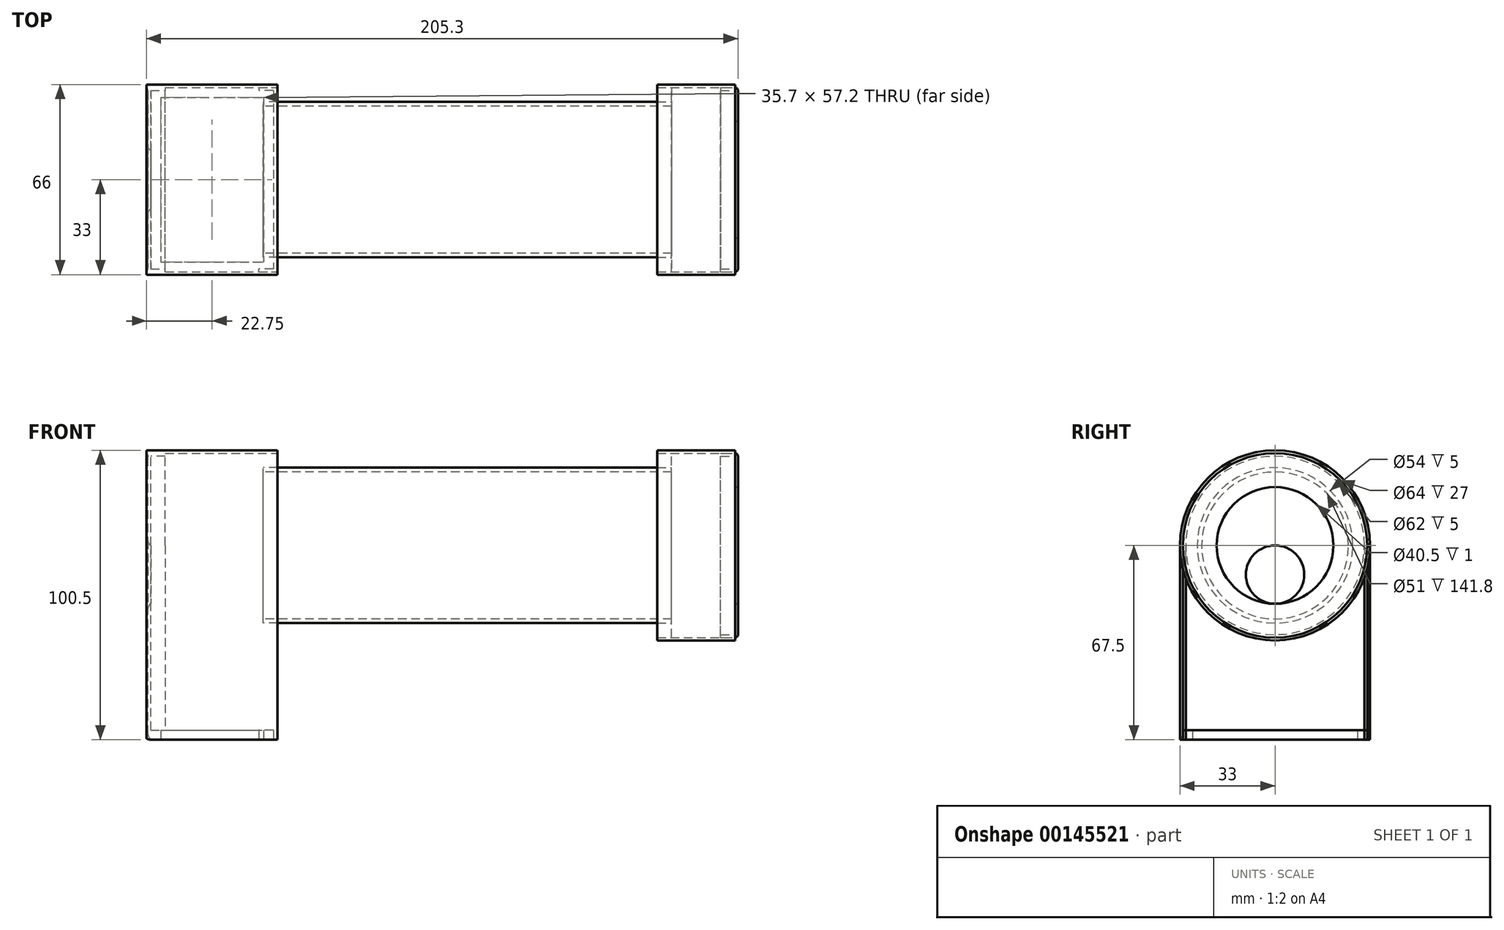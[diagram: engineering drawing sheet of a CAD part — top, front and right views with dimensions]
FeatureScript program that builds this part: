
annotation { "Feature Type Name" : "Feature", "Feature Type Description" : "" }
export const myFeature = defineFeature(function(context is Context, id is Id, definition is map)
    precondition{}
    {
        {
            assignVariable(context, id + "F0", {"name" : "CuBlech10", "anyValue" : 1});
        }
        {
            var Q0;
            Q0=qCreatedBy(makeId("Right.planeOp"),FACE);
            var sketch = newSketch(context, id + "F1", { "sketchPlane" : qUnion([Q0])});
            skCircle(sketch, "E0", {"center": v(0, 0) * mm, "radius": 27 * mm});
            skCircle(sketch, "E1", {"center": v(0, 0) * mm, "radius": 25.5 * mm});
            skSolve(sketch);
        }
        {
            var Q0;
            Q0 = qSketchRegion(id + "F1", true);
            extrude(context, id + "F2", {"entities" : qUnion([Q0]), "depth" : 141.8 * mm});
        }
        {
            var Q0;
            Q0=makeQuery(id+"F2.opExtrude","CAP_FACE",FACE,{"disambiguationData":[OSD([sQuery(id+"F1.wireOp",EDGE,"E0"),sQuery(id+"F1.wireOp",EDGE,"E1")])],"isStart":true});
            var sketch = newSketch(context, id + "F3", { "sketchPlane" : qUnion([Q0])});
            skLineSegment(sketch, "E2", {"start": v(-23.38, -13.5) * mm, "end": v(-22.08, -12.75) * mm});
            skLineSegment(sketch, "E3", {"start": v(22.08, -12.75) * mm, "end": v(23.38, -13.5) * mm});
            skLineSegment(sketch, "E4", {"start": v(0, 0) * mm, "end": v(0, -29.7) * mm, "construction": true});
            skArc(sketch, "E5", {"start": v(-22.08, -12.75) * mm, "mid": v(0, -25.5) * mm, "end": v(22.08, -12.75) * mm});
            skArc(sketch, "E6", {"start": v(-23.38, -13.5) * mm, "mid": v(0, -27) * mm, "end": v(23.38, -13.5) * mm});
            skSolve(sketch);
        }
        {
            var Q0;
            Q0=qCreatedBy(makeId("Front.planeOp"),FACE);
            var sketch = newSketch(context, id + "F4", { "sketchPlane" : qUnion([Q0])});
            skLineSegment(sketch, "E7", {"start": v(172.96, 0) * mm, "end": v(133.05, 0) * mm, "construction": true});
            skLineSegment(sketch, "E8.bottom", {"start": v(136.8, 32) * mm, "end": v(141.8, 32) * mm});
            skLineSegment(sketch, "E8.top", {"start": v(136.8, 27) * mm, "end": v(141.8, 27) * mm});
            skLineSegment(sketch, "E8.left", {"start": v(136.8, 32) * mm, "end": v(136.8, 27) * mm});
            skLineSegment(sketch, "E8.right", {"start": v(141.8, 32) * mm, "end": v(141.8, 27) * mm});
            skLineSegment(sketch, "E9.top", {"start": v(136.8, 33) * mm, "end": v(163.8, 33) * mm});
            skLineSegment(sketch, "E9.left", {"start": v(136.8, 32) * mm, "end": v(136.8, 33) * mm});
            skLineSegment(sketch, "E9.right", {"start": v(163.8, 32) * mm, "end": v(163.8, 33) * mm});
            skLineSegment(sketch, "E10.top", {"start": v(164.8, 20.25) * mm, "end": v(163.8, 20.25) * mm});
            skLineSegment(sketch, "E10.left", {"start": v(164.8, 32) * mm, "end": v(164.8, 20.25) * mm});
            skLineSegment(sketch, "E10.right", {"start": v(158.8, 32) * mm, "end": v(158.8, 31) * mm});
            skLineSegment(sketch, "E11.top", {"start": v(158.8, 31) * mm, "end": v(163.8, 31) * mm});
            skLineSegment(sketch, "E11.right", {"start": v(163.8, 20.25) * mm, "end": v(163.8, 31) * mm});
            skLineSegment(sketch, "E12", {"start": v(158.8, 32) * mm, "end": v(164.8, 32) * mm});
            skLineSegment(sketch, "E13", {"start": v(163.8, 32) * mm, "end": v(136.8, 32) * mm});
            skSolve(sketch);
        }
        {
            var Q0;
            Q0=makeQuery(id+"F4.imprint","IMPRINT",FACE,{"disambiguationData":[TD([[makeQuery(id+"F4.imprint","IMPRINT",EDGE,{"derivedFrom":sQuery(id+"F4.wireOp",EDGE,"E8.top")}),1.0]])]});
            var Q1;
            Q1=sQuery(id+"F4.wireOp",EDGE,"E7");
            revolve(context, id + "F5", {"entities" : qUnion([Q0]), "axis" : qUnion([Q1]), "revolveType" : RevolveType.FULL});
        }
        {
            var Q0;
            Q0=makeQuery(id+"F4.imprint","IMPRINT",FACE,{"disambiguationData":[TD([[makeQuery(id+"F4.imprint","IMPRINT",EDGE,{"derivedFrom":sQuery(id+"F4.wireOp",EDGE,"E9.top")}),-1.0]])]});
            var Q1;
            Q1=sQuery(id+"F4.wireOp",EDGE,"E7");
            revolve(context, id + "F6", {"entities" : qUnion([Q0]), "axis" : qUnion([Q1]), "revolveType" : RevolveType.FULL});
        }
        {
            var Q0;
            Q0=makeQuery(id+"F4.imprint","IMPRINT",FACE,{"disambiguationData":[TD([[makeQuery(id+"F4.imprint","IMPRINT",EDGE,{"derivedFrom":sQuery(id+"F4.wireOp",EDGE,"E10.top")}),-1.0]])]});
            var Q1;
            Q1=sQuery(id+"F4.wireOp",EDGE,"E7");
            revolve(context, id + "F7", {"entities" : qUnion([Q0]), "axis" : qUnion([Q1]), "revolveType" : RevolveType.FULL});
        }
        {
            var Q0;
            Q0=makeQuery(id+"F7.opRevolve","SWEPT_EDGE",EDGE,{"disambiguationData":[OSD([sQuery(id+"F4.wireOp",EDGE,"E10.left"),sQuery(id+"F4.wireOp",EDGE,"E12")])]});
            fillet(context, id + "F8", {"entities" : qUnion([Q0]), "radius" : 1 * mm, "tangentPropagation" : true, "allowEdgeOverflow" : false});
        }
        {
            var Q0;
            Q0=makeQuery(id+"F2.opExtrude","CAP_FACE",FACE,{"disambiguationData":[OSD([sQuery(id+"F1.wireOp",EDGE,"E0"),sQuery(id+"F1.wireOp",EDGE,"E1")])],"isStart":true});
            cPlane(context, id + "F9", {"entities" : qUnion([Q0]), "cplaneType" : CPlaneType.OFFSET, "offset" : 5 * mm, "oppositeDirection" : true, "width" : 150 * mm, "height" : 150 * mm});
        }
        {
            var Q0;
            Q0=qCreatedBy(id+"F9.planeOp",FACE);
            var sketch = newSketch(context, id + "F10", { "sketchPlane" : qUnion([Q0])});
            skArc(sketch, "E14", {"start": v(32, 0) * mm, "mid": v(0, 32) * mm, "end": v(-32, 0) * mm});
            skArc(sketch, "E15", {"start": v(33, 0) * mm, "mid": v(0, 33) * mm, "end": v(-33, 0) * mm});
            skLineSegment(sketch, "E16", {"start": v(-31.44, 0) * mm, "end": v(31.77, 0) * mm, "construction": true});
            skLineSegment(sketch, "E17.bottom", {"start": v(-33, 0) * mm, "end": v(-32, 0) * mm});
            skLineSegment(sketch, "E17.top", {"start": v(-33, -67.5) * mm, "end": v(-32, -67.5) * mm});
            skLineSegment(sketch, "E17.left", {"start": v(-33, 0) * mm, "end": v(-33, -67.5) * mm});
            skLineSegment(sketch, "E17.right", {"start": v(-32, 0) * mm, "end": v(-32, -67.5) * mm});
            skLineSegment(sketch, "E18.bottom", {"start": v(33, 0) * mm, "end": v(32, 0) * mm});
            skLineSegment(sketch, "E18.top", {"start": v(33, -67.5) * mm, "end": v(32, -67.5) * mm});
            skLineSegment(sketch, "E18.left", {"start": v(33, 0) * mm, "end": v(33, -67.5) * mm});
            skLineSegment(sketch, "E18.right", {"start": v(32, 0) * mm, "end": v(32, -67.5) * mm});
            skSolve(sketch);
        }
        {
            var Q0;
            Q0 = qSketchRegion(id + "F10", true);
            extrude(context, id + "F11", {"entities" : qUnion([Q0]), "depth" : 45.5 * mm});
        }
        {
            var Q0;
            Q0=makeQuery(id+"F11.opExtrude","SWEPT_FACE",FACE,{"disambiguationData":[OSD([sQuery(id+"F10.wireOp",EDGE,"E18.top")])]});
            var sketch = newSketch(context, id + "F12", { "sketchPlane" : qUnion([Q0])});
            skLineSegment(sketch, "E19.bottom", {"start": v(-39, -32) * mm, "end": v(3.5, -32) * mm});
            skLineSegment(sketch, "E19.top", {"start": v(-39, 32) * mm, "end": v(3.5, 32) * mm});
            skLineSegment(sketch, "E19.left", {"start": v(-39, -32) * mm, "end": v(-39, 32) * mm});
            skLineSegment(sketch, "E19.right", {"start": v(3.5, -32) * mm, "end": v(3.5, 32) * mm});
            skLineSegment(sketch, "E20.bottom", {"start": v(-35.6, -28.6) * mm, "end": v(0.1, -28.6) * mm});
            skLineSegment(sketch, "E20.top", {"start": v(-35.6, 28.6) * mm, "end": v(0.1, 28.6) * mm});
            skLineSegment(sketch, "E20.left", {"start": v(-35.6, -28.6) * mm, "end": v(-35.6, 28.6) * mm});
            skLineSegment(sketch, "E20.right", {"start": v(0.1, -28.6) * mm, "end": v(0.1, 28.6) * mm});
            skLineSegment(sketch, "E21", {"start": v(-39, -28.6) * mm, "end": v(-35.6, -28.6) * mm, "construction": true});
            skLineSegment(sketch, "E22", {"start": v(3.5, 28.6) * mm, "end": v(0.1, 28.6) * mm, "construction": true});
            skLineSegment(sketch, "E23", {"start": v(0.1, 28.6) * mm, "end": v(0.1, 32) * mm, "construction": true});
            skLineSegment(sketch, "E24", {"start": v(-35.6, -28.6) * mm, "end": v(-35.6, -32) * mm, "construction": true});
            skSolve(sketch);
        }
        {
            var Q0;
            Q0=makeQuery(id+"F12.imprint","IMPRINT",FACE,{"disambiguationData":[TD([[makeQuery(id+"F12.imprint","IMPRINT",EDGE,{"derivedFrom":sQuery(id+"F12.wireOp",EDGE,"E19.bottom")}),1.0]])]});
            extrude(context, id + "F13", {"entities" : qUnion([Q0]), "oppositeDirection" : true, "depth" : 3.4 * mm});
        }
        {
            var Q0;
            Q0=makeQuery(id+"F13.opExtrude","SWEPT_FACE",FACE,{"disambiguationData":[OSD([sQuery(id+"F12.wireOp",EDGE,"E19.left")])]});
            var sketch = newSketch(context, id + "F14", { "sketchPlane" : qUnion([Q0])});
            skArc(sketch, "E25", {"start": v(32, 0) * mm, "mid": v(0, 32) * mm, "end": v(-32, 0) * mm});
            skLineSegment(sketch, "E26.bottom", {"start": v(-32, -67.5) * mm, "end": v(32, -67.5) * mm});
            skLineSegment(sketch, "E26.left", {"start": v(-32, -67.5) * mm, "end": v(-32, 0) * mm});
            skLineSegment(sketch, "E26.right", {"start": v(32, -67.5) * mm, "end": v(32, 0) * mm});
            skCircle(sketch, "E27", {"center": v(0, -10.12) * mm, "radius": 10.12 * mm});
            skLineSegment(sketch, "E28", {"start": v(-4.05, 0) * mm, "end": v(17.04, 0) * mm, "construction": true});
            skSolve(sketch);
        }
        {
            var Q0;
            {var subQ2=sQuery(id+"F14.wireOp",EDGE,"E25");Q0=makeQuery(id+"F14.imprint","IMPRINT",FACE,{"disambiguationData":[TD([[makeQuery(id+"F14.imprint","IMPRINT",EDGE,{"derivedFrom":subQ2}),1.0]])]});}
            var Q1;
            {var subQ0=sQuery(id+"F14.wireOp",EDGE,"E26.bottom");Q1=makeQuery(id+"F14.imprint","IMPRINT",FACE,{"disambiguationData":[TD([[makeQuery(id+"F14.imprint","IMPRINT",EDGE,{"derivedFrom":subQ0}),1.0]])]});}
            extrude(context, id + "F15", {"entities" : qUnion([Q0, Q1]), "depth" : (getVariable(context, 'CuBlech10')) * mm});
        }
        {
            var Q0;
            Q0=makeQuery(id+"F13.opExtrude","CAP_FACE",FACE,{"disambiguationData":[OSD([sQuery(id+"F12.wireOp",EDGE,"E19.bottom"),sQuery(id+"F12.wireOp",EDGE,"E19.top"),sQuery(id+"F12.wireOp",EDGE,"E19.left"),sQuery(id+"F12.wireOp",EDGE,"E19.right"),sQuery(id+"F12.wireOp",EDGE,"E20.bottom"),sQuery(id+"F12.wireOp",EDGE,"E20.top"),sQuery(id+"F12.wireOp",EDGE,"E20.left"),sQuery(id+"F12.wireOp",EDGE,"E20.right")])],"isStart":true});
            var sketch = newSketch(context, id + "F16", { "sketchPlane" : qUnion([Q0])});
            skLineSegment(sketch, "E29.bottom", {"start": v(-39, 32) * mm, "end": v(-34, 32) * mm});
            skLineSegment(sketch, "E29.top", {"start": v(-39, 31) * mm, "end": v(-34, 31) * mm});
            skLineSegment(sketch, "E29.left", {"start": v(-39, 32) * mm, "end": v(-39, 31) * mm});
            skLineSegment(sketch, "E29.right", {"start": v(-34, 32) * mm, "end": v(-34, 31) * mm});
            skLineSegment(sketch, "E30.bottom", {"start": v(3.5, 32) * mm, "end": v(-1.5, 32) * mm});
            skLineSegment(sketch, "E30.top", {"start": v(3.5, 31) * mm, "end": v(-1.5, 31) * mm});
            skLineSegment(sketch, "E30.left", {"start": v(3.5, 32) * mm, "end": v(3.5, 31) * mm});
            skLineSegment(sketch, "E30.right", {"start": v(-1.5, 32) * mm, "end": v(-1.5, 31) * mm});
            skLineSegment(sketch, "E31.bottom", {"start": v(-39, -32) * mm, "end": v(-34, -32) * mm});
            skLineSegment(sketch, "E31.top", {"start": v(-39, -31) * mm, "end": v(-34, -31) * mm});
            skLineSegment(sketch, "E31.left", {"start": v(-39, -32) * mm, "end": v(-39, -31) * mm});
            skLineSegment(sketch, "E31.right", {"start": v(-34, -32) * mm, "end": v(-34, -31) * mm});
            skLineSegment(sketch, "E32.bottom", {"start": v(3.5, -32) * mm, "end": v(-1.5, -32) * mm});
            skLineSegment(sketch, "E32.top", {"start": v(3.5, -31) * mm, "end": v(-1.5, -31) * mm});
            skLineSegment(sketch, "E32.left", {"start": v(3.5, -32) * mm, "end": v(3.5, -31) * mm});
            skLineSegment(sketch, "E32.right", {"start": v(-1.5, -32) * mm, "end": v(-1.5, -31) * mm});
            skSolve(sketch);
        }
        {
            var Q0;
            Q0 = qSketchRegion(id + "F16", true);
            extrude(context, id + "F17", {"entities" : qUnion([Q0]), "operationType" : NewBodyOperationType.REMOVE, "oppositeDirection" : true, "depth" : 25 * mm});
        }
        {
            var Q0;
            Q0=makeQuery(id+"F15.opExtrude","SWEPT_FACE",FACE,{"disambiguationData":[OSD([sQuery(id+"F14.wireOp",EDGE,"E26.bottom")])]});
            var sketch = newSketch(context, id + "F18", { "sketchPlane" : qUnion([Q0])});
            skLineSegment(sketch, "E33.bottom", {"start": v(-39, 32) * mm, "end": v(-34, 32) * mm});
            skLineSegment(sketch, "E33.top", {"start": v(-39, 31) * mm, "end": v(-34, 31) * mm});
            skLineSegment(sketch, "E33.left", {"start": v(-39, 32) * mm, "end": v(-39, 31) * mm});
            skLineSegment(sketch, "E33.right", {"start": v(-34, 32) * mm, "end": v(-34, 31) * mm});
            skSolve(sketch);
        }
        {
            var Q0;
            Q0=makeQuery(id+"F18.imprint","IMPRINT",FACE,{"disambiguationData":[TD([[makeQuery(id+"F18.imprint","IMPRINT",EDGE,{"derivedFrom":sQuery(id+"F18.wireOp",EDGE,"E33.bottom")}),-1.0]])]});
            var Q1;
            Q1=makeQuery(id+"F15.opExtrude","CAP_EDGE",EDGE,{"disambiguationData":[OSD([sQuery(id+"F14.wireOp",EDGE,"E26.right")])],"isStart":true});
            var Q2;
            Q2=makeQuery(id+"F15.opExtrude","CAP_EDGE",EDGE,{"disambiguationData":[OSD([sQuery(id+"F14.wireOp",EDGE,"E25")])],"isStart":true});
            var Q3;
            Q3=makeQuery(id+"F15.opExtrude","CAP_EDGE",EDGE,{"disambiguationData":[OSD([sQuery(id+"F14.wireOp",EDGE,"E26.left")])],"isStart":true});
            sweep(context, id + "F19", {"operationType" : NewBodyOperationType.ADD, "profiles" : qUnion([Q0]), "path" : qUnion([Q1, Q2, Q3])});
        }
        {
            var Q0;
            Q0=makeQuery(id+"F15.opExtrude","CAP_FACE",FACE,{"disambiguationData":[OSD([sQuery(id+"F14.wireOp",EDGE,"E25"),sQuery(id+"F14.wireOp",EDGE,"E26.bottom"),sQuery(id+"F14.wireOp",EDGE,"E26.left"),sQuery(id+"F14.wireOp",EDGE,"E26.right"),sQuery(id+"F14.wireOp",EDGE,"E27")])],"isStart":false});
            fillet(context, id + "F20", {"entities" : qUnion([Q0]), "radius" : 2 * mm, "tangentPropagation" : true, "allowEdgeOverflow" : false});
        }
    });
